# Revit family: ledbatten-e_l12-19_38w-dali-830_840-em1_531000020400_0dfc
name_source: partatom
category: Lighting Fixtures
units: mm (PartAtom-declared; Revit-internal decimal feet)

## family parameters
Cut with Voids When Loaded = No
Host = Face
Light Source = No
Part Type = Normal
Room Calculation Point = No
Round Connector Dimension = Use Diameter
Shared = No

## types (1)
- LEDBatten-E L12-19/38W-DALI-830/840-EM1 (1 x LED, 5700 lm, 4000)
    Apparent Load = 19 VA
    Approval mark = CE
    CIE Flux Codes = 44 73 91 89 99
    Color Rendering = 80
    Color Temperature = 4000
    Control Gear = Electronic ballast
    Default Elevation = 1800 mm
    Description = Batten EcoMax 1128mm-38W-2850/5700lm-3/4000K-DALI-Emergency 1h
    Frequency = 60 Hz
    Height = 74 mm
    Lamp = 1 x LED
    Lamp Light Flux = 5700 lm
    Lamp count = 1
    Length = 1128 mm
    Luminous efficacy = 297 lm/W
    Manufacturer = OPPLE
    ModVariant = No
    Model = 531000020400
    Mounting Place = Ceiling
    Mounting Type = Surface mounted
    Number of Poles = 1
    OnlyDefault = Yes
    Power Factor = 1
    Product Name = LEDBatten-E L12-19/38W-DALI-830/840-EM1
    Product group = Ceiling mounted luminaire
    ProductGroupID = 3
    Protection Class = Protection class I
    Protection Degree = IP 20
    RLX_Detail_Level = 1
    RLX_Emergency_Light_Flux = 0 lm
    RLX_Emergency_Type = 0
    RLX_Emergency_Type_DB = No
    RlxData = <blob elided: 95149 chars, md5=ecd185c6>
    Socket = socket
    Standby Power = 0 W
    System Light Flux = 5637 lm
    System Power = 19 W
    Type Comments = Product without accessories
    Type Image = web_bat_ip20.jpg
    URL = http://relux.com
    VarID = ---
    Voltage = 230 V
    Voltage Range = 220-240 V
    Weight = 0.00 kg
    Width = 63 mm

## geometry (parser evidence)
native form markers: Blend x4, Sweep x13
no freeform markers — native parametric forms only
